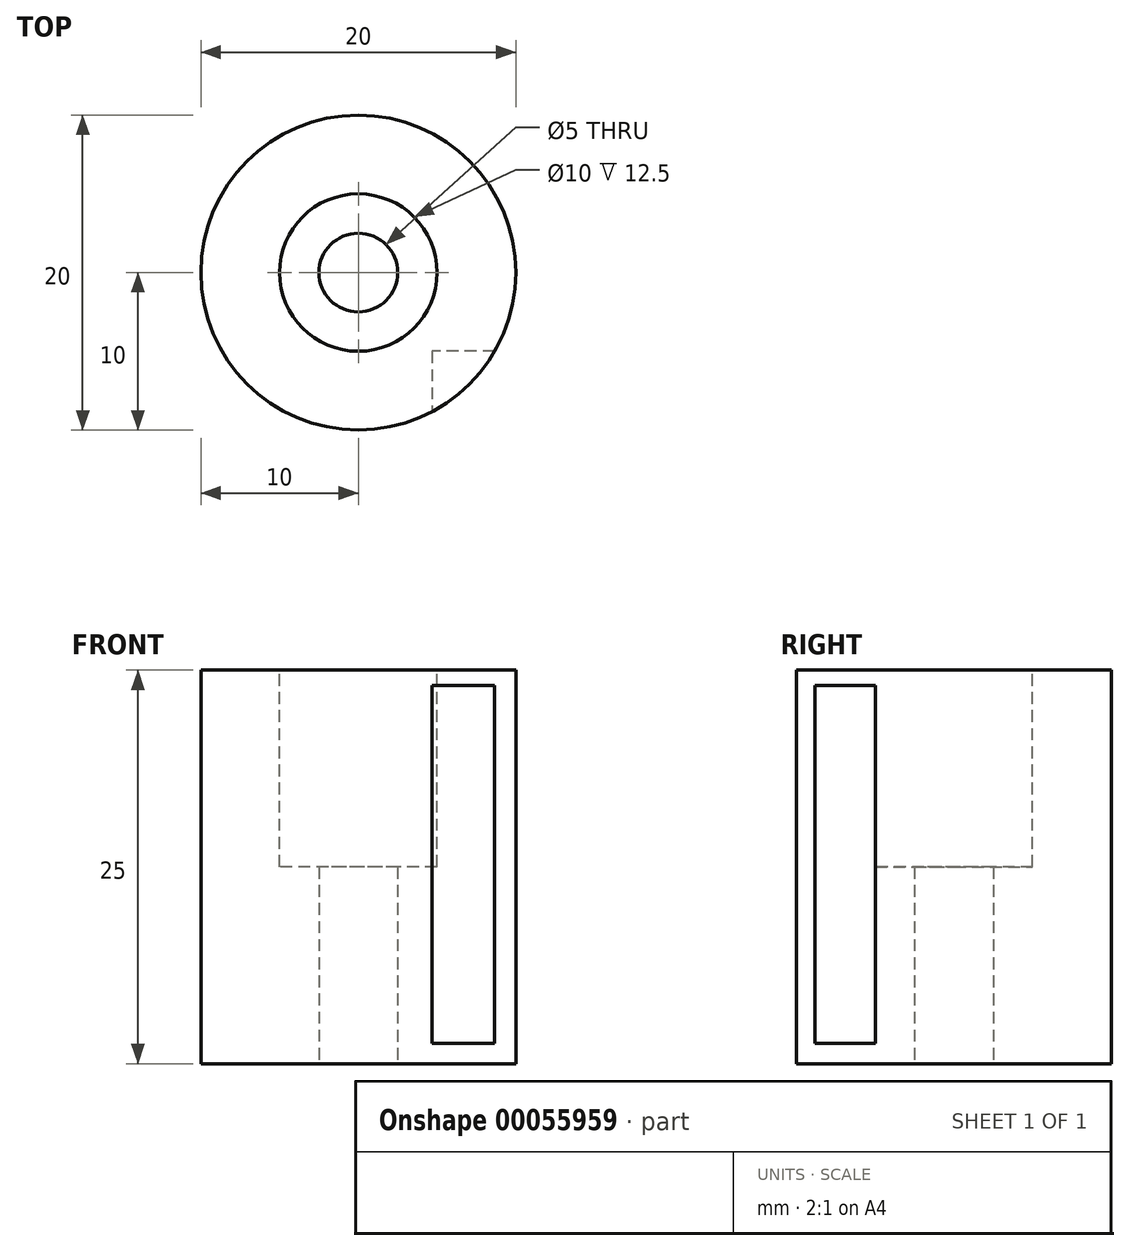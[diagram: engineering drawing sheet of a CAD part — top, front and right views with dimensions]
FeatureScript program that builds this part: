
annotation { "Feature Type Name" : "Feature", "Feature Type Description" : "" }
export const myFeature = defineFeature(function(context is Context, id is Id, definition is map)
    precondition{}
    {
        {
            var Q0;
            Q0=qCreatedBy(makeId("Top.planeOp"),FACE);
            var sketch = newSketch(context, id + "F0", { "sketchPlane" : qUnion([Q0])});
            skCircle(sketch, "E0", {"center": v(0, 0) * mm, "radius": 10 * mm});
            skCircle(sketch, "E1", {"center": v(0, 0) * mm, "radius": 2.5 * mm});
            skSolve(sketch);
        }
        {
            var Q0;
            Q0=makeQuery(id+"F0.imprint","IMPRINT",FACE,{"disambiguationData":[TD([[makeQuery(id+"F0.imprint","IMPRINT",EDGE,{"derivedFrom":sQuery(id+"F0.wireOp",EDGE,"E0")}),1.0]])]});
            extrude(context, id + "F1", {"entities" : qUnion([Q0]), "depth" : 25 * mm});
        }
        {
            var Q0;
            Q0=makeQuery(id+"F1.opExtrude","CAP_FACE",FACE,{"disambiguationData":[OSD([sQuery(id+"F0.wireOp",EDGE,"E0")])],"isStart":false});
            var sketch = newSketch(context, id + "F2", { "sketchPlane" : qUnion([Q0])});
            skCircle(sketch, "E2", {"center": v(0, 0) * mm, "radius": 5 * mm});
            skSolve(sketch);
        }
        {
            var Q0;
            Q0=makeQuery(id+"F2.imprint","IMPRINT",FACE,{"disambiguationData":[TD([[makeQuery(id+"F2.imprint","IMPRINT",EDGE,{"derivedFrom":sQuery(id+"F2.wireOp",EDGE,"E2")}),1.0]])]});
            extrude(context, id + "F3", {"entities" : qUnion([Q0]), "operationType" : NewBodyOperationType.REMOVE, "oppositeDirection" : true, "depth" : 12.5 * mm});
        }
        {
            var Q0;
            Q0=qCreatedBy(makeId("Front.planeOp"),FACE);
            cPlane(context, id + "F4", {"entities" : qUnion([Q0]), "cplaneType" : CPlaneType.OFFSET, "offset" : 10 * mm, "width" : 150 * mm, "height" : 150 * mm});
        }
        {
            var Q0;
            Q0=qCreatedBy(id+"F4.planeOp",FACE);
            var sketch = newSketch(context, id + "F5", { "sketchPlane" : qUnion([Q0])});
            skLineSegment(sketch, "E3.bottom", {"start": v(9.16, 24.02) * mm, "end": v(4.7, 24.02) * mm});
            skLineSegment(sketch, "E3.top", {"start": v(9.16, 1.3) * mm, "end": v(4.7, 1.3) * mm});
            skLineSegment(sketch, "E3.left", {"start": v(9.16, 24.02) * mm, "end": v(9.16, 1.3) * mm});
            skLineSegment(sketch, "E3.right", {"start": v(4.7, 24.02) * mm, "end": v(4.7, 1.3) * mm});
            skSolve(sketch);
        }
        {
            var Q0;
            Q0=makeQuery(id+"F5.imprint","IMPRINT",FACE,{"disambiguationData":[TD([[makeQuery(id+"F5.imprint","IMPRINT",EDGE,{"derivedFrom":sQuery(id+"F5.wireOp",EDGE,"E3.bottom")}),1.0]])]});
            extrude(context, id + "F6", {"entities" : qUnion([Q0]), "operationType" : NewBodyOperationType.REMOVE, "oppositeDirection" : true, "depth" : 5 * mm});
        }
    });
